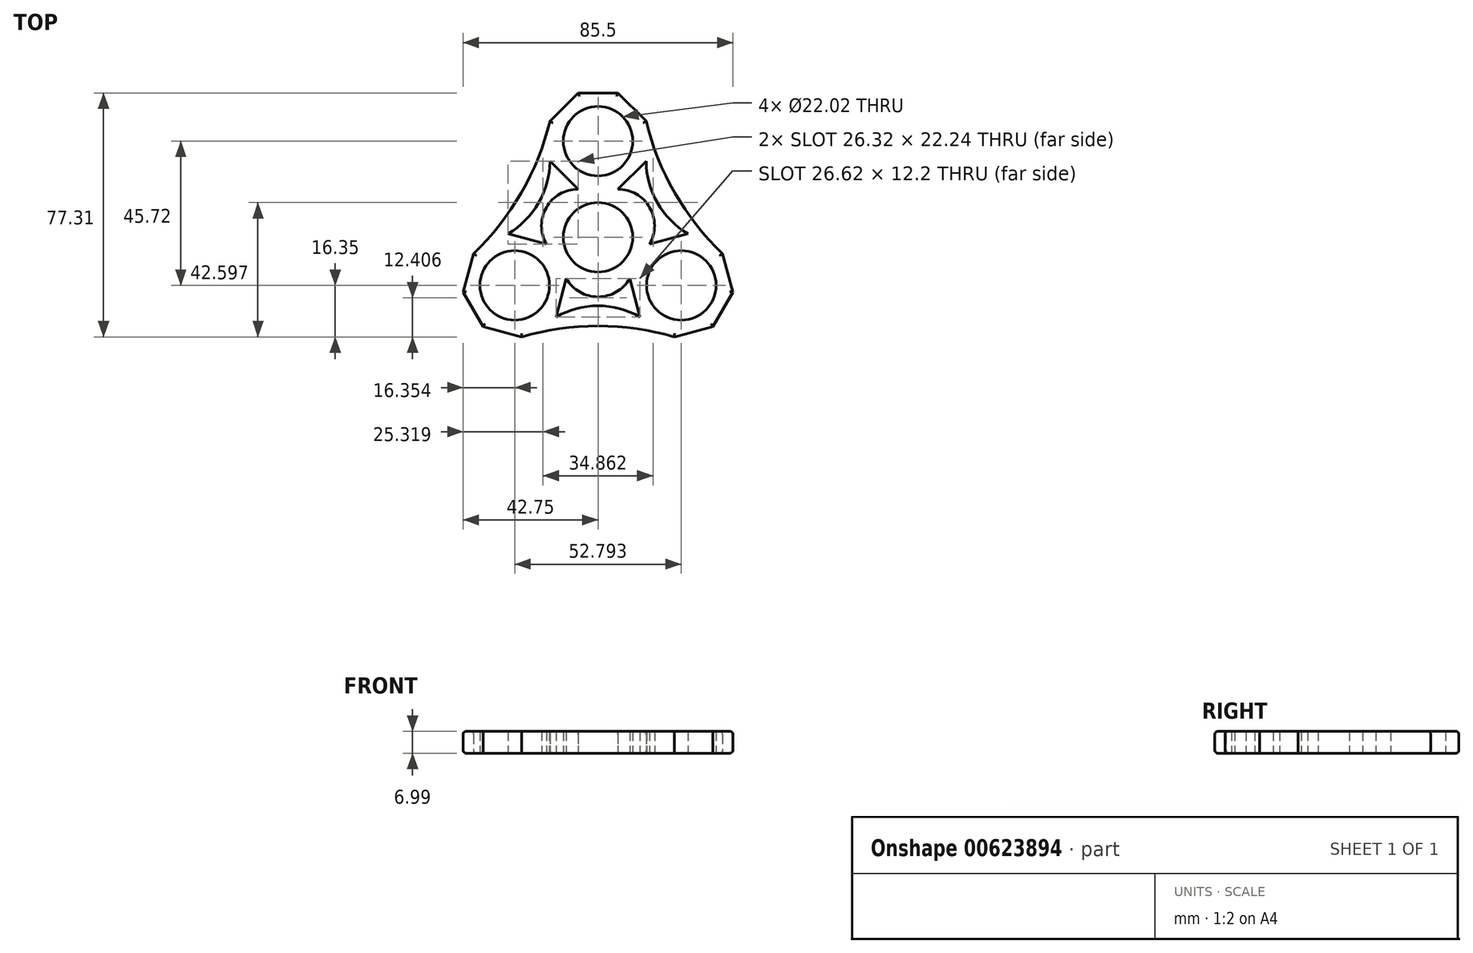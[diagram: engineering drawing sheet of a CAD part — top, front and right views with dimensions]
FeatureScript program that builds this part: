
annotation { "Feature Type Name" : "Feature", "Feature Type Description" : "" }
export const myFeature = defineFeature(function(context is Context, id is Id, definition is map)
    precondition{}
    {
        {
            var Q0;
            Q0=qCreatedBy(makeId("Top.planeOp"),FACE);
            var sketch = newSketch(context, id + "F0", { "sketchPlane" : qUnion([Q0])});
            skCircle(sketch, "E0", {"center": v(0, 0) * mm, "radius": 11.01 * mm});
            skLineSegment(sketch, "E1", {"start": v(0, 0) * mm, "end": v(0, 30.48) * mm});
            skLineSegment(sketch, "E2", {"start": v(0, 0) * mm, "end": v(-26.4, -15.24) * mm});
            skLineSegment(sketch, "E3", {"start": v(0, 0) * mm, "end": v(26.4, -15.24) * mm});
            skCircle(sketch, "E4", {"center": v(0, 30.48) * mm, "radius": 11.01 * mm});
            skCircle(sketch, "E5", {"center": v(-26.4, -15.24) * mm, "radius": 11.01 * mm});
            skCircle(sketch, "E6", {"center": v(26.4, -15.24) * mm, "radius": 11.01 * mm});
            skCircle(sketch, "E7.cCircle", {"center": v(0, 30.48) * mm, "radius": 15.24 * mm, "construction": true});
            skLineSegment(sketch, "E7.0", {"start": v(6.31, 15.24) * mm, "end": v(-6.31, 15.24) * mm});
            skLineSegment(sketch, "E7.1", {"start": v(-6.31, 15.24) * mm, "end": v(-15.24, 24.17) * mm});
            skLineSegment(sketch, "E7.2", {"start": v(-15.24, 24.17) * mm, "end": v(-15.24, 36.8) * mm});
            skLineSegment(sketch, "E7.3", {"start": v(-15.24, 36.8) * mm, "end": v(-6.31, 45.72) * mm});
            skLineSegment(sketch, "E7.4", {"start": v(-6.31, 45.72) * mm, "end": v(6.31, 45.72) * mm});
            skLineSegment(sketch, "E7.5", {"start": v(6.31, 45.72) * mm, "end": v(15.24, 36.8) * mm});
            skLineSegment(sketch, "E7.6", {"start": v(15.24, 36.8) * mm, "end": v(15.24, 24.17) * mm});
            skLineSegment(sketch, "E7.7", {"start": v(15.24, 24.17) * mm, "end": v(6.31, 15.24) * mm});
            skPoint(sketch, "E7.0.midPoint", {"position": v(0, 15.24) * mm});
            skCircle(sketch, "E8.cCircle", {"center": v(-26.4, -15.24) * mm, "radius": 15.24 * mm, "construction": true});
            skLineSegment(sketch, "E8.0", {"start": v(-16.35, -2.15) * mm, "end": v(-10.04, -13.09) * mm});
            skLineSegment(sketch, "E8.1", {"start": v(-10.04, -13.09) * mm, "end": v(-13.3, -25.28) * mm});
            skLineSegment(sketch, "E8.2", {"start": v(-13.3, -25.28) * mm, "end": v(-24.24, -31.6) * mm});
            skLineSegment(sketch, "E8.3", {"start": v(-24.24, -31.6) * mm, "end": v(-36.44, -28.33) * mm});
            skLineSegment(sketch, "E8.4", {"start": v(-36.44, -28.33) * mm, "end": v(-42.75, -17.4) * mm});
            skLineSegment(sketch, "E8.5", {"start": v(-42.75, -17.4) * mm, "end": v(-39.48, -5.2) * mm});
            skLineSegment(sketch, "E8.6", {"start": v(-39.48, -5.2) * mm, "end": v(-28.55, 1.11) * mm});
            skLineSegment(sketch, "E8.7", {"start": v(-28.55, 1.11) * mm, "end": v(-16.35, -2.15) * mm});
            skPoint(sketch, "E8.0.midPoint", {"position": v(-13.2, -7.62) * mm});
            skCircle(sketch, "E9.cCircle", {"center": v(26.4, -15.24) * mm, "radius": 15.24 * mm, "construction": true});
            skLineSegment(sketch, "E9.0", {"start": v(10.04, -13.09) * mm, "end": v(16.35, -2.15) * mm});
            skLineSegment(sketch, "E9.1", {"start": v(16.35, -2.15) * mm, "end": v(28.55, 1.11) * mm});
            skLineSegment(sketch, "E9.2", {"start": v(28.55, 1.11) * mm, "end": v(39.48, -5.2) * mm});
            skLineSegment(sketch, "E9.3", {"start": v(39.48, -5.2) * mm, "end": v(42.75, -17.4) * mm});
            skLineSegment(sketch, "E9.4", {"start": v(42.75, -17.4) * mm, "end": v(36.44, -28.33) * mm});
            skLineSegment(sketch, "E9.5", {"start": v(36.44, -28.33) * mm, "end": v(24.24, -31.6) * mm});
            skLineSegment(sketch, "E9.6", {"start": v(24.24, -31.6) * mm, "end": v(13.3, -25.28) * mm});
            skLineSegment(sketch, "E9.7", {"start": v(13.3, -25.28) * mm, "end": v(10.04, -13.09) * mm});
            skPoint(sketch, "E9.0.midPoint", {"position": v(13.2, -7.62) * mm});
            skArc(sketch, "E10", {"start": v(16.35, -2.15) * mm, "mid": v(16.35, 9.44) * mm, "end": v(6.31, 15.24) * mm});
            skArc(sketch, "E11", {"start": v(-10.04, -13.09) * mm, "mid": v(0, -18.88) * mm, "end": v(10.04, -13.09) * mm});
            skArc(sketch, "E12", {"start": v(-6.31, 15.24) * mm, "mid": v(-16.35, 9.44) * mm, "end": v(-16.35, -2.15) * mm});
            skArc(sketch, "E13", {"start": v(-28.55, 1.11) * mm, "mid": v(-18.8, 10.86) * mm, "end": v(-15.24, 24.17) * mm});
            skArc(sketch, "E14", {"start": v(15.24, 24.17) * mm, "mid": v(18.8, 10.86) * mm, "end": v(28.55, 1.11) * mm});
            skArc(sketch, "E15", {"start": v(13.3, -25.28) * mm, "mid": v(0, -21.72) * mm, "end": v(-13.3, -25.28) * mm});
            skArc(sketch, "E16", {"start": v(-39.48, -5.2) * mm, "mid": v(-24.34, 14.05) * mm, "end": v(-15.24, 36.8) * mm});
            skArc(sketch, "E17", {"start": v(15.24, 36.8) * mm, "mid": v(24.34, 14.05) * mm, "end": v(39.48, -5.2) * mm});
            skArc(sketch, "E18", {"start": v(24.24, -31.6) * mm, "mid": v(0, -28.1) * mm, "end": v(-24.24, -31.6) * mm});
            skSolve(sketch);
        }
        {
            var Q0;
            Q0=makeQuery(id+"F0.imprint","IMPRINT",FACE,{"disambiguationData":[TD([[makeQuery(id+"F0.imprint","IMPRINT",EDGE,{"derivedFrom":sQuery(id+"F0.wireOp",EDGE,"E7.2")}),1.0]])]});
            var Q1;
            Q1=makeQuery(id+"F0.imprint","IMPRINT",FACE,{"disambiguationData":[TD([[makeQuery(id+"F0.imprint","IMPRINT",EDGE,{"derivedFrom":sQuery(id+"F0.wireOp",EDGE,"E7.6")}),1.0]])]});
            var Q2;
            Q2=makeQuery(id+"F0.imprint","IMPRINT",FACE,{"disambiguationData":[TD([[makeQuery(id+"F0.imprint","IMPRINT",EDGE,{"derivedFrom":sQuery(id+"F0.wireOp",EDGE,"E8.2")}),1.0]])]});
            var Q3;
            Q3=makeQuery(id+"F0.imprint","IMPRINT",FACE,{"disambiguationData":[TD([[makeQuery(id+"F0.imprint","IMPRINT",EDGE,{"derivedFrom":sQuery(id+"F0.wireOp",EDGE,"E4")}),-1.0]])]});
            var Q4;
            Q4=makeQuery(id+"F0.imprint","IMPRINT",FACE,{"disambiguationData":[TD([[makeQuery(id+"F0.imprint","IMPRINT",EDGE,{"derivedFrom":sQuery(id+"F0.wireOp",EDGE,"E5")}),-1.0]])]});
            var Q5;
            Q5=makeQuery(id+"F0.imprint","IMPRINT",FACE,{"disambiguationData":[TD([[makeQuery(id+"F0.imprint","IMPRINT",EDGE,{"derivedFrom":sQuery(id+"F0.wireOp",EDGE,"E6")}),-1.0]])]});
            var Q6;
            {var subQ0=sQuery(id+"F0.wireOp",EDGE,"E12");Q6=makeQuery(id+"F0.imprint","IMPRINT",FACE,{"disambiguationData":[TD([[makeQuery(id+"F0.imprint","IMPRINT",EDGE,{"derivedFrom":subQ0}),1.0]])]});}
            var Q7;
            {var subQ9=sQuery(id+"F0.wireOp",EDGE,"E10");Q7=makeQuery(id+"F0.imprint","IMPRINT",FACE,{"disambiguationData":[TD([[makeQuery(id+"F0.imprint","IMPRINT",EDGE,{"derivedFrom":subQ9}),1.0]])]});}
            var Q8;
            {var subQ0=sQuery(id+"F0.wireOp",EDGE,"E11");Q8=makeQuery(id+"F0.imprint","IMPRINT",FACE,{"disambiguationData":[TD([[makeQuery(id+"F0.imprint","IMPRINT",EDGE,{"derivedFrom":subQ0}),1.0]])]});}
            extrude(context, id + "F1", {"entities" : qUnion([Q0, Q1, Q2, Q3, Q4, Q5, Q6, Q7, Q8]), "depth" : 7 * mm, "offsetDistance" : 25.4 * mm});
        }
        {
            var Q0;
            Q0=makeQuery(id+"F1.opExtrude","CAP_EDGE",EDGE,{"disambiguationData":[OSD([sQuery(id+"F0.wireOp",EDGE,"E18")])],"isStart":false});
            var Q1;
            Q1=makeQuery(id+"F1.opExtrude","CAP_EDGE",EDGE,{"disambiguationData":[OSD([sQuery(id+"F0.wireOp",EDGE,"E18")])],"isStart":true});
            var Q2;
            Q2=makeQuery(id+"F1.opExtrude","CAP_EDGE",EDGE,{"disambiguationData":[OSD([sQuery(id+"F0.wireOp",EDGE,"E16")])],"isStart":true});
            var Q3;
            Q3=makeQuery(id+"F1.opExtrude","CAP_EDGE",EDGE,{"disambiguationData":[OSD([sQuery(id+"F0.wireOp",EDGE,"E16")])],"isStart":false});
            var Q4;
            Q4=makeQuery(id+"F1.opExtrude","CAP_EDGE",EDGE,{"disambiguationData":[OSD([sQuery(id+"F0.wireOp",EDGE,"E17")])],"isStart":true});
            var Q5;
            Q5=makeQuery(id+"F1.opExtrude","CAP_EDGE",EDGE,{"disambiguationData":[OSD([sQuery(id+"F0.wireOp",EDGE,"E17")])],"isStart":false});
            var Q6;
            Q6=makeQuery(id+"F1.opExtrude","CAP_EDGE",EDGE,{"disambiguationData":[OSD([sQuery(id+"F0.wireOp",EDGE,"E7.3")])],"isStart":false});
            var Q7;
            Q7=makeQuery(id+"F1.opExtrude","CAP_EDGE",EDGE,{"disambiguationData":[OSD([sQuery(id+"F0.wireOp",EDGE,"E7.4")])],"isStart":false});
            var Q8;
            Q8=makeQuery(id+"F1.opExtrude","CAP_EDGE",EDGE,{"disambiguationData":[OSD([sQuery(id+"F0.wireOp",EDGE,"E7.5")])],"isStart":false});
            var Q9;
            Q9=makeQuery(id+"F1.opExtrude","CAP_EDGE",EDGE,{"disambiguationData":[OSD([sQuery(id+"F0.wireOp",EDGE,"E7.5")])],"isStart":true});
            var Q10;
            Q10=makeQuery(id+"F1.opExtrude","CAP_EDGE",EDGE,{"disambiguationData":[OSD([sQuery(id+"F0.wireOp",EDGE,"E7.4")])],"isStart":true});
            var Q11;
            Q11=makeQuery(id+"F1.opExtrude","CAP_EDGE",EDGE,{"disambiguationData":[OSD([sQuery(id+"F0.wireOp",EDGE,"E7.3")])],"isStart":true});
            var Q12;
            Q12=makeQuery(id+"F1.opExtrude","CAP_EDGE",EDGE,{"disambiguationData":[OSD([sQuery(id+"F0.wireOp",EDGE,"E8.4")])],"isStart":false});
            var Q13;
            Q13=makeQuery(id+"F1.opExtrude","CAP_EDGE",EDGE,{"disambiguationData":[OSD([sQuery(id+"F0.wireOp",EDGE,"E8.3")])],"isStart":false});
            var Q14;
            Q14=makeQuery(id+"F1.opExtrude","CAP_EDGE",EDGE,{"disambiguationData":[OSD([sQuery(id+"F0.wireOp",EDGE,"E8.3")])],"isStart":true});
            var Q15;
            Q15=makeQuery(id+"F1.opExtrude","CAP_EDGE",EDGE,{"disambiguationData":[OSD([sQuery(id+"F0.wireOp",EDGE,"E8.4")])],"isStart":true});
            var Q16;
            Q16=makeQuery(id+"F1.opExtrude","CAP_EDGE",EDGE,{"disambiguationData":[OSD([sQuery(id+"F0.wireOp",EDGE,"E8.5")])],"isStart":true});
            var Q17;
            Q17=makeQuery(id+"F1.opExtrude","CAP_EDGE",EDGE,{"disambiguationData":[OSD([sQuery(id+"F0.wireOp",EDGE,"E8.5")])],"isStart":false});
            var Q18;
            Q18=makeQuery(id+"F1.opExtrude","CAP_EDGE",EDGE,{"disambiguationData":[OSD([sQuery(id+"F0.wireOp",EDGE,"E9.5")])],"isStart":false});
            var Q19;
            Q19=makeQuery(id+"F1.opExtrude","CAP_EDGE",EDGE,{"disambiguationData":[OSD([sQuery(id+"F0.wireOp",EDGE,"E9.5")])],"isStart":true});
            var Q20;
            Q20=makeQuery(id+"F1.opExtrude","CAP_EDGE",EDGE,{"disambiguationData":[OSD([sQuery(id+"F0.wireOp",EDGE,"E9.4")])],"isStart":true});
            var Q21;
            Q21=makeQuery(id+"F1.opExtrude","CAP_EDGE",EDGE,{"disambiguationData":[OSD([sQuery(id+"F0.wireOp",EDGE,"E9.4")])],"isStart":false});
            var Q22;
            Q22=makeQuery(id+"F1.opExtrude","CAP_EDGE",EDGE,{"disambiguationData":[OSD([sQuery(id+"F0.wireOp",EDGE,"E9.3")])],"isStart":false});
            var Q23;
            Q23=makeQuery(id+"F1.opExtrude","CAP_EDGE",EDGE,{"disambiguationData":[OSD([sQuery(id+"F0.wireOp",EDGE,"E9.3")])],"isStart":true});
            fillet(context, id + "F2", {"entities" : qUnion([Q0, Q1, Q2, Q3, Q4, Q5, Q6, Q7, Q8, Q9, Q10, Q11, Q12, Q13, Q14, Q15, Q16, Q17, Q18, Q19, Q20, Q21, Q22, Q23]), "radius" : 1.02 * mm, "tangentPropagation" : true, "allowEdgeOverflow" : false});
        }
    });
